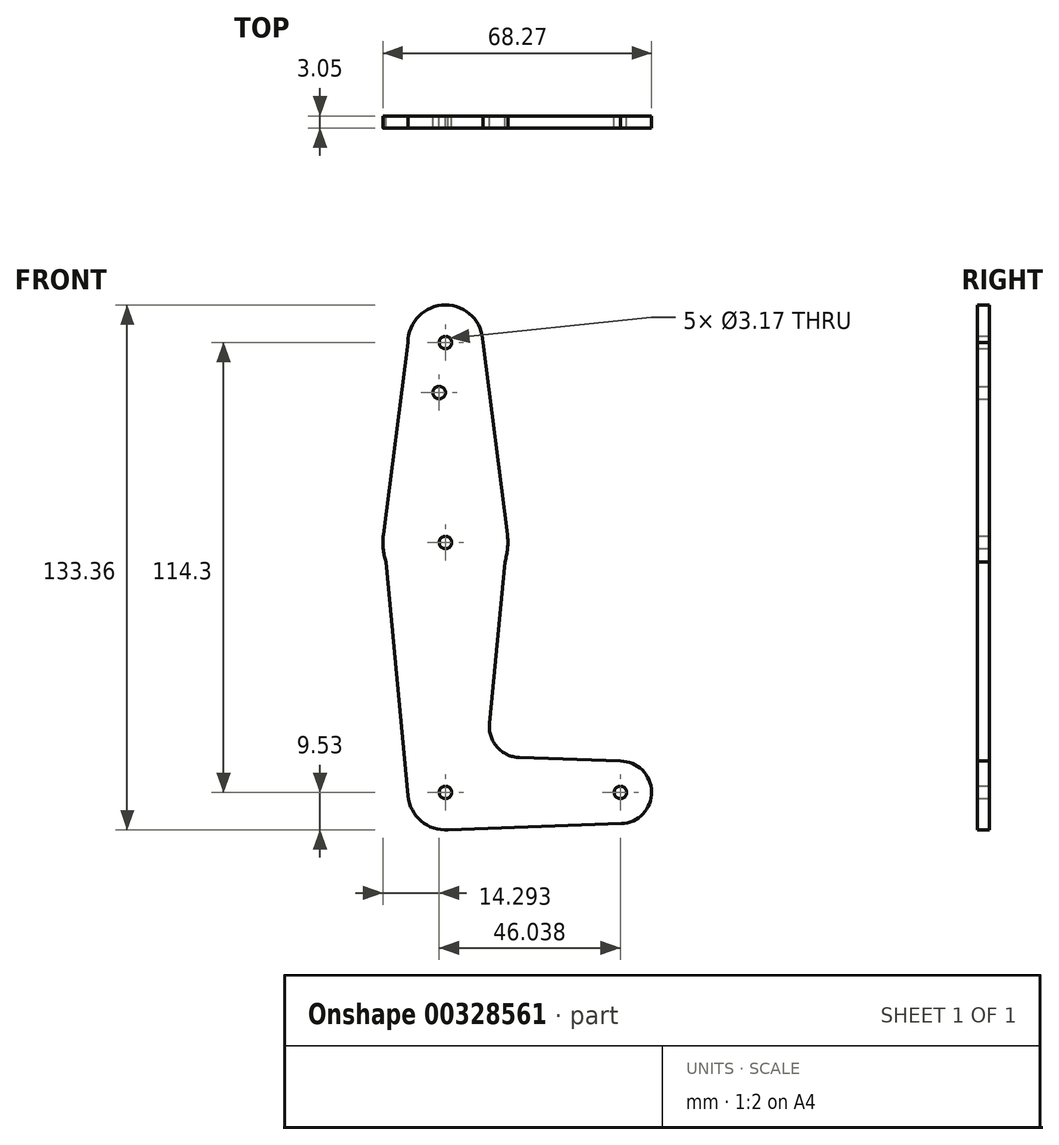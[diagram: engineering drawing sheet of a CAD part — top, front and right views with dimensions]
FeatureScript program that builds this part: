
annotation { "Feature Type Name" : "Feature", "Feature Type Description" : "" }
export const myFeature = defineFeature(function(context is Context, id is Id, definition is map)
    precondition{}
    {
        {
            var Q0;
            Q0=qCreatedBy(makeId("Front.planeOp"),FACE);
            var sketch = newSketch(context, id + "F0", { "sketchPlane" : qUnion([Q0])});
            skLineSegment(sketch, "E0", {"start": v(0, 114.3) * mm, "end": v(0, 0) * mm, "construction": true});
            skLineSegment(sketch, "E1", {"start": v(0, 0) * mm, "end": v(44.45, 0) * mm, "construction": true});
            skCircle(sketch, "E2", {"center": v(44.45, 0) * mm, "radius": 7.94 * mm});
            skCircle(sketch, "E3", {"center": v(0, 0) * mm, "radius": 9.53 * mm});
            skCircle(sketch, "E4", {"center": v(0, 114.3) * mm, "radius": 9.53 * mm});
            skCircle(sketch, "E5", {"center": v(0, 63.5) * mm, "radius": 15.88 * mm});
            skLineSegment(sketch, "E6", {"start": v(9.53, 114.3) * mm, "end": v(15.75, 65.5) * mm});
            skLineSegment(sketch, "E7", {"start": v(-9.53, 114.3) * mm, "end": v(-15.75, 65.5) * mm});
            skLineSegment(sketch, "E8", {"start": v(15.75, 65.5) * mm, "end": v(11.2, 17.55) * mm});
            skLineSegment(sketch, "E9", {"start": v(-15.75, 65.5) * mm, "end": v(-9.48, -0.9) * mm});
            skLineSegment(sketch, "E10", {"start": v(18.82, 8.85) * mm, "end": v(44.45, 7.94) * mm});
            skLineSegment(sketch, "E11", {"start": v(0, -9.53) * mm, "end": v(44.73, -7.93) * mm});
            skCircle(sketch, "E12", {"center": v(0, 114.3) * mm, "radius": 1.59 * mm});
            skCircle(sketch, "E13", {"center": v(0, 63.5) * mm, "radius": 1.59 * mm});
            skCircle(sketch, "E14", {"center": v(0, 0) * mm, "radius": 1.59 * mm});
            skCircle(sketch, "E15", {"center": v(44.45, 0) * mm, "radius": 1.59 * mm});
            skArc(sketch, "E16.filletArc", {"start": v(11.2, 17.55) * mm, "mid": v(13.13, 11.55) * mm, "end": v(18.82, 8.85) * mm});
            skCircle(sketch, "E17", {"center": v(-1.59, 101.58) * mm, "radius": 1.59 * mm});
            skSolve(sketch);
        }
        {
            var Q0;
            Q0 = qSketchRegion(id + "F0", true);
            extrude(context, id + "F1", {"entities" : qUnion([Q0]), "depth" : 3.05 * mm});
        }
    });
